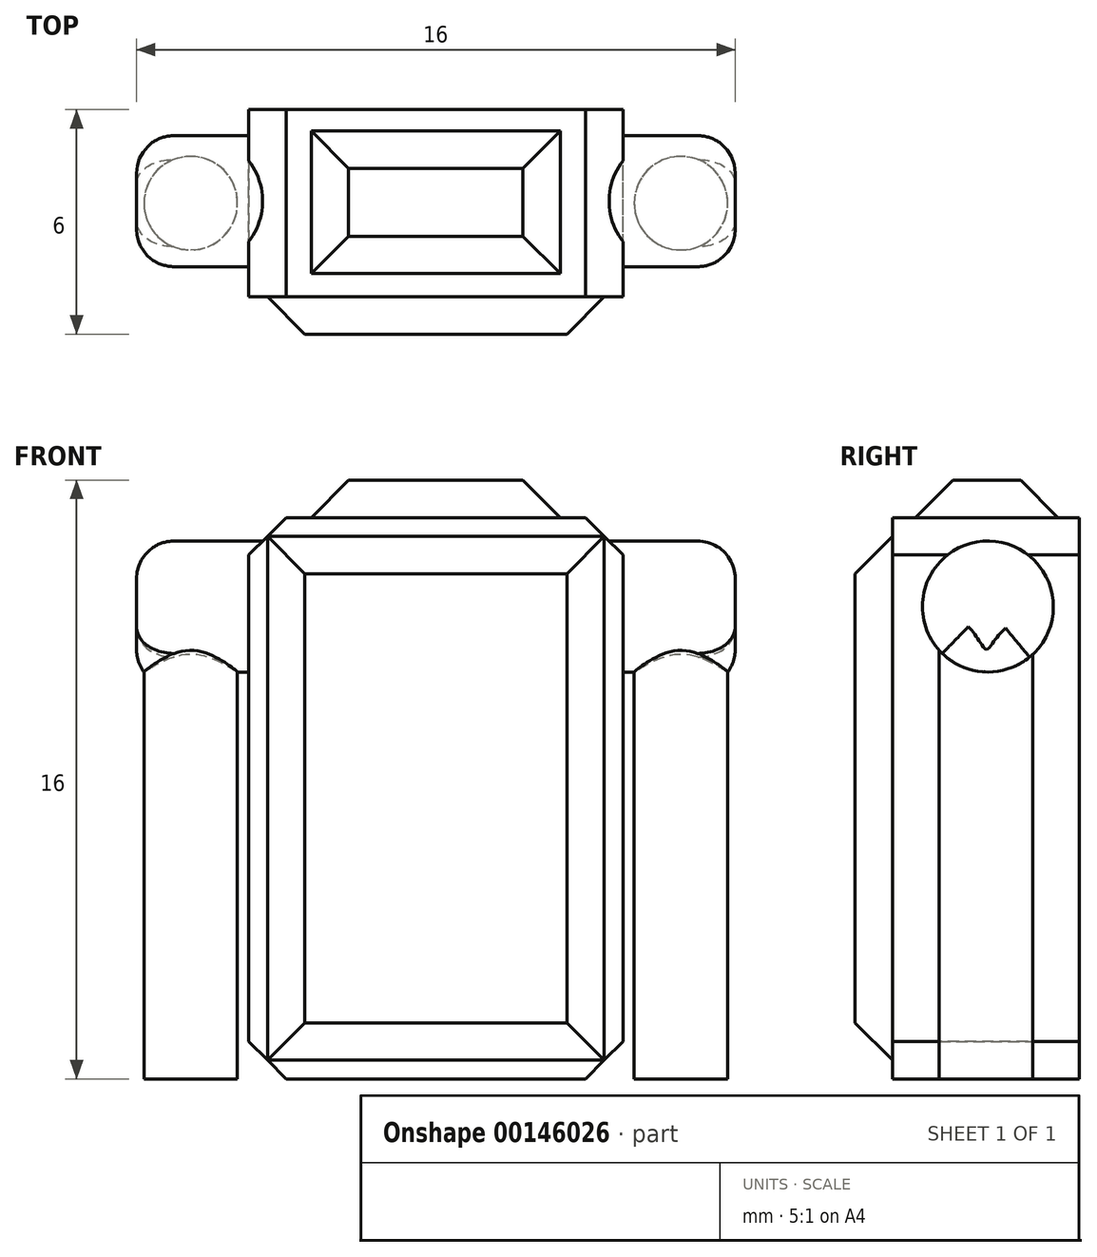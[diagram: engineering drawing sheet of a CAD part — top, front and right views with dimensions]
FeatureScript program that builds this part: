
annotation { "Feature Type Name" : "Feature", "Feature Type Description" : "" }
export const myFeature = defineFeature(function(context is Context, id is Id, definition is map)
    precondition{}
    {
        {
            var Q0;
            Q0=qCreatedBy(makeId("Front.planeOp"),FACE);
            var sketch = newSketch(context, id + "F0", { "sketchPlane" : qUnion([Q0])});
            skLineSegment(sketch, "E0.bottom", {"start": v(5, 7.5) * mm, "end": v(-5, 7.5) * mm});
            skLineSegment(sketch, "E0.top", {"start": v(5, -7.5) * mm, "end": v(-5, -7.5) * mm});
            skLineSegment(sketch, "E0.left", {"start": v(5, 7.5) * mm, "end": v(5, -7.5) * mm});
            skLineSegment(sketch, "E0.right", {"start": v(-5, 7.5) * mm, "end": v(-5, -7.5) * mm});
            skPoint(sketch, "E0.middle", {"position": v(0, 0) * mm});
            skSolve(sketch);
        }
        {
            var Q0;
            Q0 = qSketchRegion(id + "F0", true);
            extrude(context, id + "F1", {"entities" : qUnion([Q0]), "depth" : 5 * mm});
        }
        {
            var Q0;
            Q0=qCreatedBy(makeId("Right.planeOp"),FACE);
            var sketch = newSketch(context, id + "F2", { "sketchPlane" : qUnion([Q0])});
            skCircle(sketch, "E1", {"center": v(-2.45, 5.12) * mm, "radius": 1.75 * mm});
            skSolve(sketch);
        }
        {
            var Q0;
            Q0 = qSketchRegion(id + "F2", true);
            extrude(context, id + "F3", {"entities" : qUnion([Q0]), "operationType" : NewBodyOperationType.ADD, "endBound" : BoundingType.SYMMETRIC, "depth" : 16 * mm});
        }
        {
            var Q0;
            Q0=makeQuery(id+"F1.opExtrude","SWEPT_FACE",FACE,{"disambiguationData":[OSD([sQuery(id+"F0.wireOp",EDGE,"E0.top")])]});
            var sketch = newSketch(context, id + "F4", { "sketchPlane" : qUnion([Q0])});
            skCircle(sketch, "E2", {"center": v(-6.55, 2.5) * mm, "radius": 1.25 * mm});
            skPoint(sketch, "E2.centerSnap0", {"position": v(-5, 2.5) * mm});
            skCircle(sketch, "E3.MirrorC", {"center": v(6.55, 2.5) * mm, "radius": 1.25 * mm});
            skSolve(sketch);
        }
        {
            var Q0;
            Q0 = qSketchRegion(id + "F4", true);
            extrude(context, id + "F5", {"entities" : qUnion([Q0]), "operationType" : NewBodyOperationType.ADD, "oppositeDirection" : true, "depth" : 12.85 * mm});
        }
        {
            var Q0;
            Q0=makeQuery(id+"F3.opExtrude","CAP_EDGE",EDGE,{"disambiguationData":[OSD([sQuery(id+"F2.wireOp",EDGE,"E1")])],"isStart":true});
            fillet(context, id + "F6", {"entities" : qUnion([Q0]), "radius" : 1 * mm, "tangentPropagation" : true, "allowEdgeOverflow" : false});
        }
        {
            var Q0;
            Q0=makeQuery(id+"F3.opExtrude","CAP_EDGE",EDGE,{"disambiguationData":[OSD([sQuery(id+"F2.wireOp",EDGE,"E1")])],"isStart":false});
            fillet(context, id + "F7", {"entities" : qUnion([Q0]), "radius" : 1 * mm, "tangentPropagation" : true, "allowEdgeOverflow" : false});
        }
        {
            var Q0;
            Q0=makeQuery(id+"F1.opExtrude","CAP_FACE",FACE,{"disambiguationData":[OSD([sQuery(id+"F0.wireOp",EDGE,"E0.bottom"),sQuery(id+"F0.wireOp",EDGE,"E0.top"),sQuery(id+"F0.wireOp",EDGE,"E0.left"),sQuery(id+"F0.wireOp",EDGE,"E0.right")])],"isStart":false});
            var sketch = newSketch(context, id + "F8", { "sketchPlane" : qUnion([Q0])});
            skLineSegment(sketch, "E4.bottom", {"start": v(4.5, 7) * mm, "end": v(-4.5, 7) * mm});
            skLineSegment(sketch, "E4.top", {"start": v(4.5, -7) * mm, "end": v(-4.5, -7) * mm});
            skLineSegment(sketch, "E4.left", {"start": v(4.5, 7) * mm, "end": v(4.5, -7) * mm});
            skLineSegment(sketch, "E4.right", {"start": v(-4.5, 7) * mm, "end": v(-4.5, -7) * mm});
            skPoint(sketch, "E4.middle", {"position": v(0, 0) * mm});
            skSolve(sketch);
        }
        {
            var Q0;
            Q0 = qSketchRegion(id + "F8", true);
            extrude(context, id + "F9", {"entities" : qUnion([Q0]), "operationType" : NewBodyOperationType.ADD, "depth" : 1 * mm});
        }
        {
            var Q0;
            Q0=makeQuery(id+"F9.opExtrude","CAP_EDGE",EDGE,{"disambiguationData":[OSD([sQuery(id+"F8.wireOp",EDGE,"E4.right")])],"isStart":false});
            var Q1;
            Q1=makeQuery(id+"F9.opExtrude","CAP_EDGE",EDGE,{"disambiguationData":[OSD([sQuery(id+"F8.wireOp",EDGE,"E4.bottom")])],"isStart":false});
            var Q2;
            Q2=makeQuery(id+"F9.opExtrude","CAP_EDGE",EDGE,{"disambiguationData":[OSD([sQuery(id+"F8.wireOp",EDGE,"E4.left")])],"isStart":false});
            var Q3;
            Q3=makeQuery(id+"F9.opExtrude","CAP_EDGE",EDGE,{"disambiguationData":[OSD([sQuery(id+"F8.wireOp",EDGE,"E4.top")])],"isStart":false});
            chamfer(context, id + "F10", {"entities" : qUnion([Q0, Q1, Q2, Q3]), "width" : 1 * mm, "tangentPropagation" : true});
        }
        {
            var Q0;
            Q0=makeQuery(id+"F1.opExtrude","SWEPT_EDGE",EDGE,{"disambiguationData":[OSD([sQuery(id+"F0.wireOp",EDGE,"E0.top"),sQuery(id+"F0.wireOp",EDGE,"E0.left")])]});
            var Q1;
            Q1=makeQuery(id+"F1.opExtrude","SWEPT_EDGE",EDGE,{"disambiguationData":[OSD([sQuery(id+"F0.wireOp",EDGE,"E0.top"),sQuery(id+"F0.wireOp",EDGE,"E0.right")])]});
            var Q2;
            Q2=makeQuery(id+"F1.opExtrude","SWEPT_EDGE",EDGE,{"disambiguationData":[OSD([sQuery(id+"F0.wireOp",EDGE,"E0.bottom"),sQuery(id+"F0.wireOp",EDGE,"E0.left")])]});
            var Q3;
            Q3=makeQuery(id+"F1.opExtrude","SWEPT_EDGE",EDGE,{"disambiguationData":[OSD([sQuery(id+"F0.wireOp",EDGE,"E0.bottom"),sQuery(id+"F0.wireOp",EDGE,"E0.right")])]});
            chamfer(context, id + "F11", {"entities" : qUnion([Q0, Q1, Q2, Q3]), "width" : 1 * mm, "tangentPropagation" : true});
        }
        {
            var Q0;
            Q0=makeQuery(id+"F1.opExtrude","SWEPT_FACE",FACE,{"disambiguationData":[OSD([sQuery(id+"F0.wireOp",EDGE,"E0.bottom")])]});
            var sketch = newSketch(context, id + "F12", { "sketchPlane" : qUnion([Q0])});
            skLineSegment(sketch, "E5.bottom", {"start": v(-3.33, -0.57) * mm, "end": v(0, -0.57) * mm});
            skLineSegment(sketch, "E5.top", {"start": v(-3.33, -4.38) * mm, "end": v(0, -4.38) * mm});
            skLineSegment(sketch, "E5.left", {"start": v(-3.33, -0.57) * mm, "end": v(-3.33, -4.38) * mm});
            skLineSegment(sketch, "E6.MirrorCS", {"start": v(3.33, -0.57) * mm, "end": v(0, -0.57) * mm});
            skLineSegment(sketch, "E7.MirrorCS", {"start": v(3.33, -0.57) * mm, "end": v(3.33, -4.38) * mm});
            skLineSegment(sketch, "E8.MirrorCS", {"start": v(3.33, -4.38) * mm, "end": v(0, -4.38) * mm});
            skSolve(sketch);
        }
        {
            var Q0;
            Q0 = qSketchRegion(id + "F12", true);
            extrude(context, id + "F13", {"entities" : qUnion([Q0]), "operationType" : NewBodyOperationType.ADD, "depth" : 1 * mm});
        }
        {
            var Q0;
            Q0=makeQuery(id+"F13.opExtrude","CAP_EDGE",EDGE,{"disambiguationData":[OSD([sQuery(id+"F12.wireOp",EDGE,"E5.top"),sQuery(id+"F12.wireOp",EDGE,"E8.MirrorCS")])],"isStart":false});
            var Q1;
            Q1=makeQuery(id+"F13.opExtrude","CAP_EDGE",EDGE,{"disambiguationData":[OSD([sQuery(id+"F12.wireOp",EDGE,"E7.MirrorCS")])],"isStart":false});
            var Q2;
            Q2=makeQuery(id+"F13.opExtrude","CAP_EDGE",EDGE,{"disambiguationData":[OSD([sQuery(id+"F12.wireOp",EDGE,"E5.left")])],"isStart":false});
            var Q3;
            Q3=makeQuery(id+"F13.opExtrude","CAP_EDGE",EDGE,{"disambiguationData":[OSD([sQuery(id+"F12.wireOp",EDGE,"E5.bottom"),sQuery(id+"F12.wireOp",EDGE,"E6.MirrorCS")])],"isStart":false});
            chamfer(context, id + "F14", {"entities" : qUnion([Q0, Q1, Q2, Q3]), "width" : 1 * mm, "tangentPropagation" : true});
        }
    });
